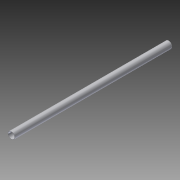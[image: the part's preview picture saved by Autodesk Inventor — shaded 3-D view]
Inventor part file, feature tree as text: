
AUTODESK INVENTOR PART (.ipt)
format: ipt  version: 2014 (Build 180170000, 170)  size: 75,776 bytes
history: native  units: in
note: dims shown in document units (in); Inventor stores cm internally (conversion verified against a paired STEP export)
features: extrude x2, sketch x2
ambient origin geometry x8: Origin, YZ Plane, XZ Plane, XY Plane, X Axis, Y Axis, Z Axis, Center Point
bodies: Solid1 (feature_tree)
feature tree (4):
  extrude  "Extrusion1"  Depth=0.1181in
  extrude  "Extrusion2"  Depth=180.3937in TaperAngle=0.0deg
  sketch  "Sketch1"  dims[d0=2.4803in d1=0.1181in]
  sketch  "Sketch2"  dims[d2=236.2205in d3=0.0in d4=180.3937in d5=0.0in]
